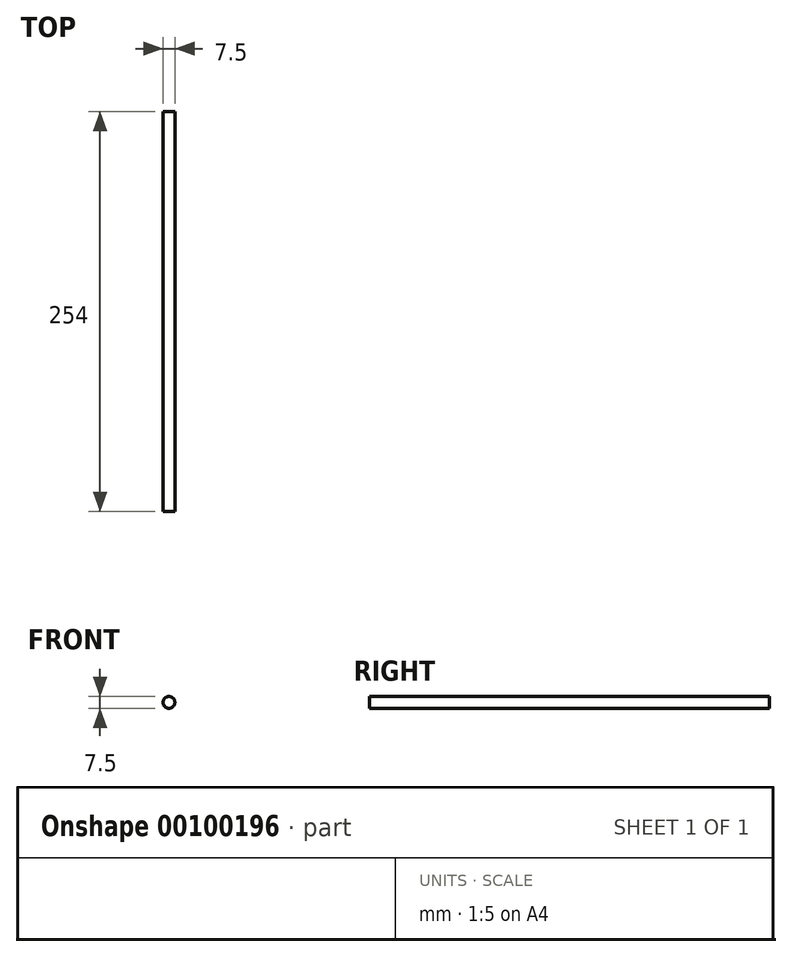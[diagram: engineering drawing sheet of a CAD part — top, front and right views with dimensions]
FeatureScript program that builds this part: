
annotation { "Feature Type Name" : "Feature", "Feature Type Description" : "" }
export const myFeature = defineFeature(function(context is Context, id is Id, definition is map)
    precondition{}
    {
        {
            var Q0;
            Q0=qCreatedBy(makeId("Front.planeOp"),FACE);
            var sketch = newSketch(context, id + "F0", { "sketchPlane" : qUnion([Q0])});
            skCircle(sketch, "E0", {"center": v(0, 0) * mm, "radius": 3.75 * mm});
            skSolve(sketch);
        }
        {
            var Q0;
            Q0=makeQuery(id+"F0.imprint","IMPRINT",FACE,{"disambiguationData":[TD([[makeQuery(id+"F0.imprint","IMPRINT",EDGE,{"derivedFrom":sQuery(id+"F0.wireOp",EDGE,"E0")}),1.0]])]});
            extrude(context, id + "F1", {"entities" : qUnion([Q0]), "depth" : 254 * mm});
        }
    });
